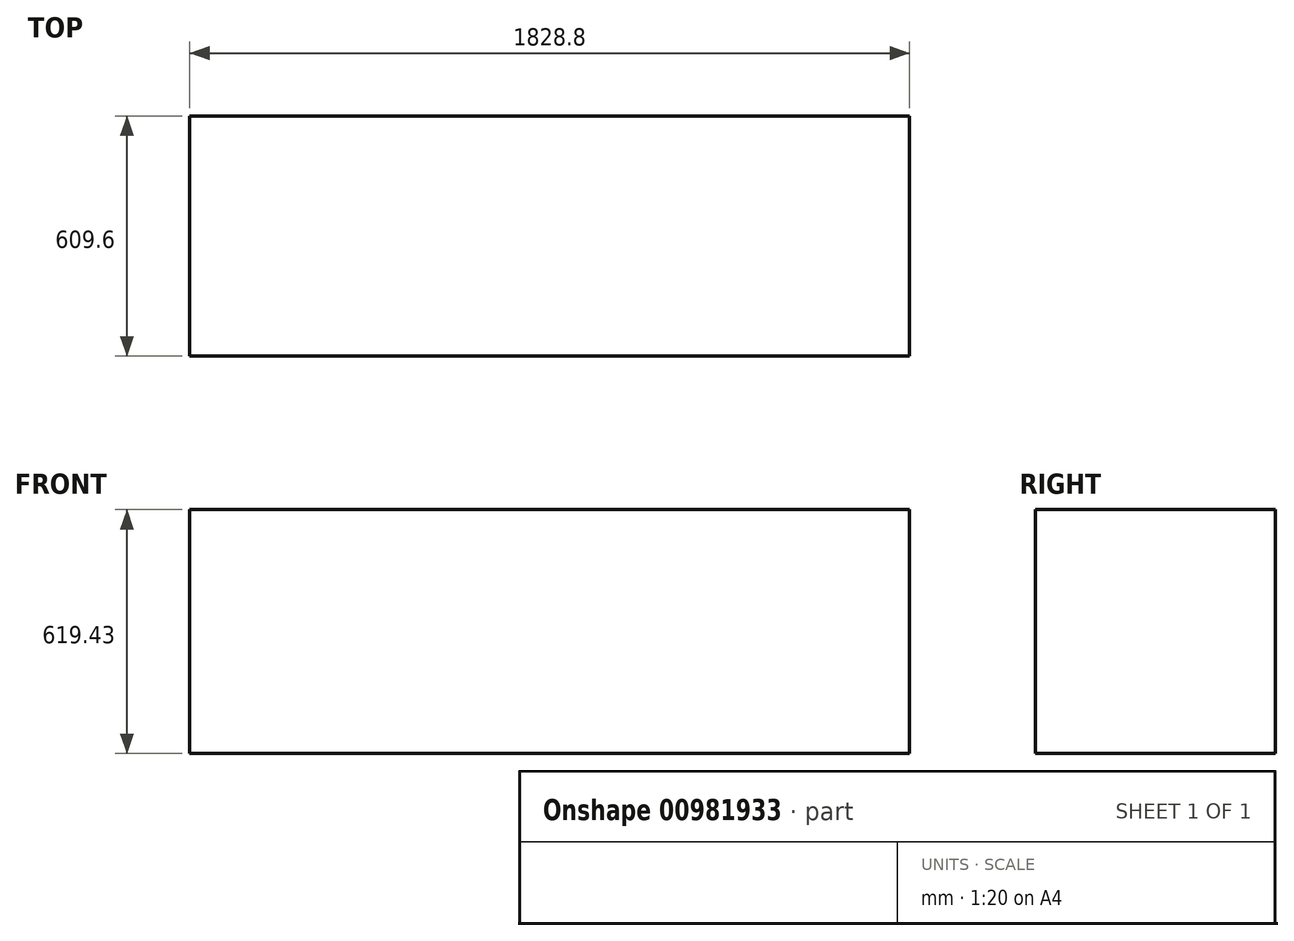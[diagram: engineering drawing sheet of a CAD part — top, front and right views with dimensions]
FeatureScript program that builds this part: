
annotation { "Feature Type Name" : "Feature", "Feature Type Description" : "" }
export const myFeature = defineFeature(function(context is Context, id is Id, definition is map)
    precondition{}
    {
        {
            var Q0;
            Q0=qCreatedBy(makeId("Front.planeOp"),FACE);
            var sketch = newSketch(context, id + "F0", { "sketchPlane" : qUnion([Q0])});
            skLineSegment(sketch, "E0.bottom", {"start": v(-914.22, 340.24) * mm, "end": v(914.58, 340.24) * mm});
            skLineSegment(sketch, "E0.top", {"start": v(-914.22, -279.2) * mm, "end": v(914.58, -279.2) * mm});
            skLineSegment(sketch, "E0.left", {"start": v(-914.22, 340.24) * mm, "end": v(-914.22, -279.2) * mm});
            skLineSegment(sketch, "E0.right", {"start": v(914.58, 340.24) * mm, "end": v(914.58, -279.2) * mm});
            skSolve(sketch);
        }
        {
            var Q0;
            Q0 = qSketchRegion(id + "F0", true);
            extrude(context, id + "F1", {"entities" : qUnion([Q0]), "depth" : 609.6 * mm, "offsetDistance" : 25.4 * mm});
        }
    });
